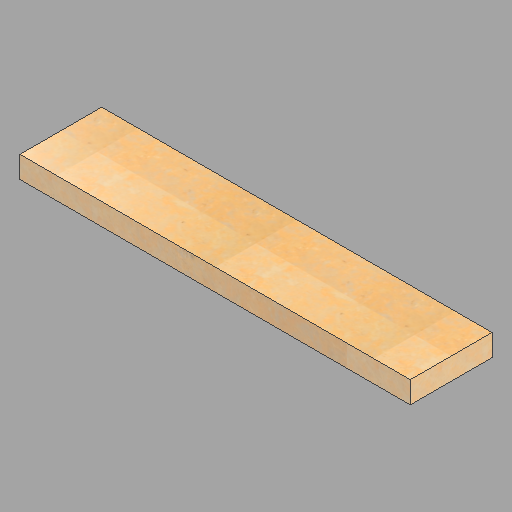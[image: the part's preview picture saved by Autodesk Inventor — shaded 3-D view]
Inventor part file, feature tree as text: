
AUTODESK INVENTOR PART (.ipt)
format: ipt  version: 2023 (Build 270158000, 158)  size: 199,168 bytes
history: native  units: in
note: dims shown in document units (in); Inventor stores cm internally (conversion verified against a paired STEP export)
features: extrude x1, sketch x1
ambient origin geometry x8: Origin, YZ Plane, XZ Plane, XY Plane, X Axis, Y Axis, Z Axis, Center Point
bodies: Solid1 (feature_tree)
feature tree (2):
  extrude  "Extrusion1"  Depth=15.0in
  sketch  "Sketch1"  dims[d0=71.625in d1=15.0in d2=4.0in d3=0.0in]
